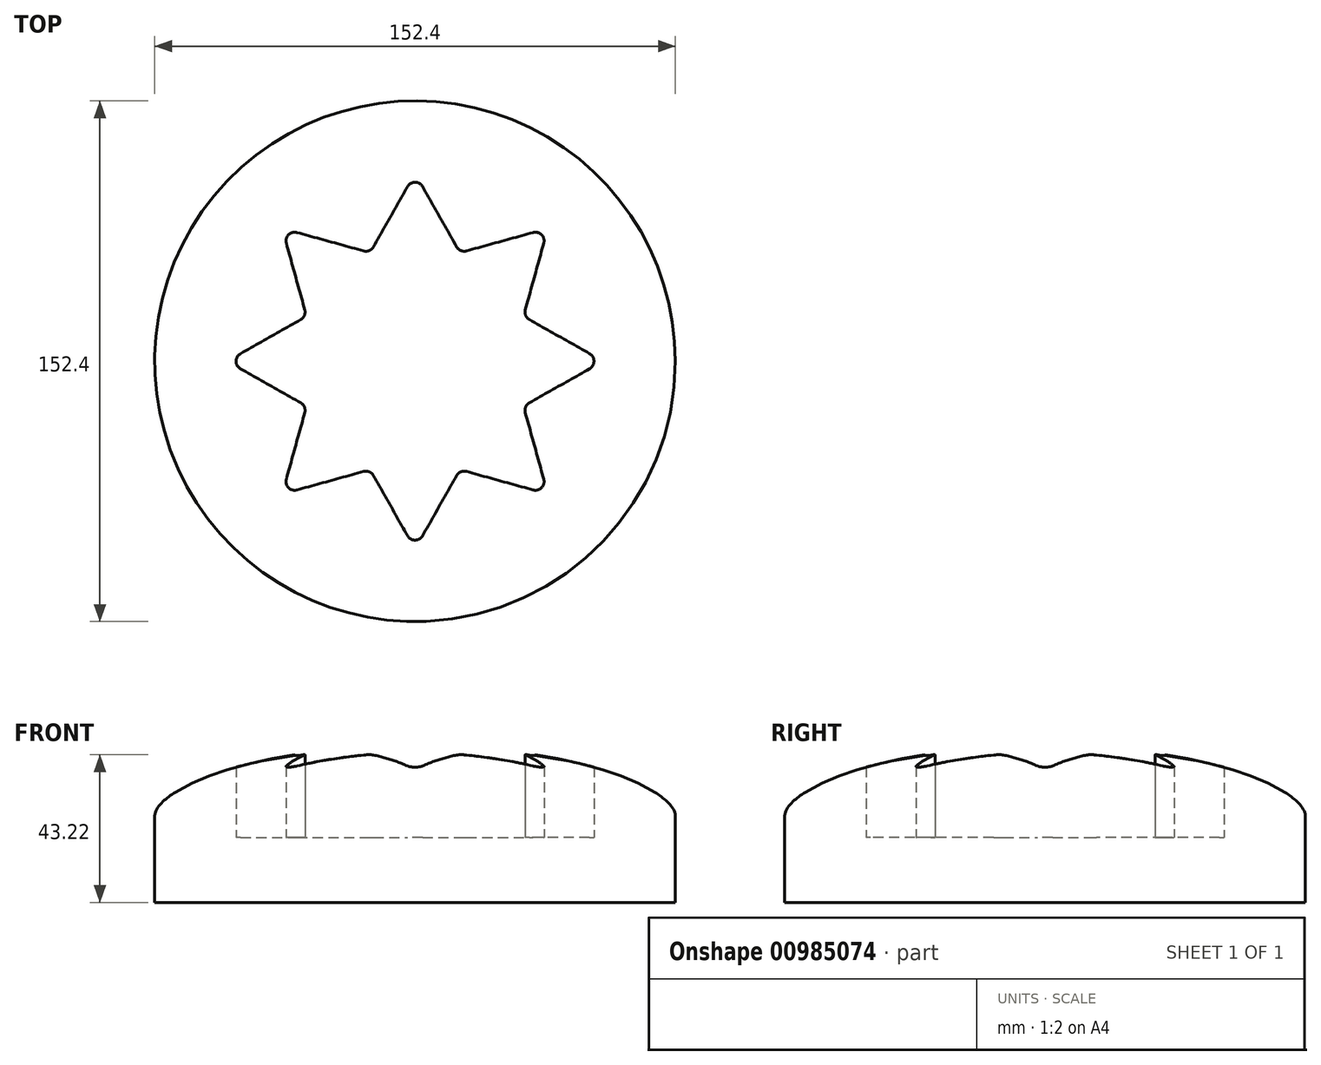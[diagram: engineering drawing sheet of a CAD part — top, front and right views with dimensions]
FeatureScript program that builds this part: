
annotation { "Feature Type Name" : "Feature", "Feature Type Description" : "" }
export const myFeature = defineFeature(function(context is Context, id is Id, definition is map)
    precondition{}
    {
        {
            var Q0;
            Q0=qCreatedBy(makeId("Top.planeOp"),FACE);
            var sketch = newSketch(context, id + "F0", { "sketchPlane" : qUnion([Q0])});
            skCircle(sketch, "E0", {"center": v(0, 0) * mm, "radius": 50.8 * mm, "construction": true});
            skCircle(sketch, "E1", {"center": v(0, 0) * mm, "radius": 31.75 * mm, "construction": true});
            skLineSegment(sketch, "E2.0", {"start": v(-13.15, 31.75) * mm, "end": v(13.15, 31.75) * mm, "construction": true});
            skLineSegment(sketch, "E2.1", {"start": v(13.15, 31.75) * mm, "end": v(31.75, 13.15) * mm, "construction": true});
            skLineSegment(sketch, "E2.2", {"start": v(31.75, 13.15) * mm, "end": v(31.75, -13.15) * mm, "construction": true});
            skLineSegment(sketch, "E2.3", {"start": v(31.75, -13.15) * mm, "end": v(13.15, -31.75) * mm, "construction": true});
            skLineSegment(sketch, "E2.4", {"start": v(13.15, -31.75) * mm, "end": v(-13.15, -31.75) * mm, "construction": true});
            skLineSegment(sketch, "E2.5", {"start": v(-13.15, -31.75) * mm, "end": v(-31.75, -13.15) * mm, "construction": true});
            skLineSegment(sketch, "E2.6", {"start": v(-31.75, -13.15) * mm, "end": v(-31.75, 13.15) * mm, "construction": true});
            skLineSegment(sketch, "E2.7", {"start": v(-31.75, 13.15) * mm, "end": v(-13.15, 31.75) * mm, "construction": true});
            skPoint(sketch, "E2.0.midPoint", {"position": v(0, 31.75) * mm});
            skLineSegment(sketch, "E3.0", {"start": v(0, 54.99) * mm, "end": v(38.88, 38.88) * mm, "construction": true});
            skLineSegment(sketch, "E3.1", {"start": v(38.88, 38.88) * mm, "end": v(54.99, 0) * mm, "construction": true});
            skLineSegment(sketch, "E3.2", {"start": v(54.99, 0) * mm, "end": v(38.88, -38.88) * mm, "construction": true});
            skLineSegment(sketch, "E3.3", {"start": v(38.88, -38.88) * mm, "end": v(0, -54.99) * mm, "construction": true});
            skLineSegment(sketch, "E3.4", {"start": v(0, -54.99) * mm, "end": v(-38.88, -38.88) * mm, "construction": true});
            skLineSegment(sketch, "E3.5", {"start": v(-38.88, -38.88) * mm, "end": v(-54.99, 0) * mm, "construction": true});
            skLineSegment(sketch, "E3.6", {"start": v(-54.99, 0) * mm, "end": v(-38.88, 38.88) * mm, "construction": true});
            skLineSegment(sketch, "E3.7", {"start": v(-38.88, 38.88) * mm, "end": v(0, 54.99) * mm, "construction": true});
            skPoint(sketch, "E3.0.midPoint", {"position": v(19.44, 46.93) * mm});
            skLineSegment(sketch, "E4", {"start": v(-12.17, 33.48) * mm, "end": v(-2.21, 51.08) * mm});
            skLineSegment(sketch, "E5", {"start": v(2.21, 51.08) * mm, "end": v(12.17, 33.48) * mm});
            skLineSegment(sketch, "E6", {"start": v(15.06, 32.28) * mm, "end": v(34.56, 37.68) * mm});
            skLineSegment(sketch, "E7", {"start": v(37.68, 34.56) * mm, "end": v(32.28, 15.06) * mm});
            skLineSegment(sketch, "E8", {"start": v(33.48, 12.17) * mm, "end": v(51.08, 2.21) * mm});
            skLineSegment(sketch, "E9", {"start": v(51.08, -2.21) * mm, "end": v(33.48, -12.17) * mm});
            skLineSegment(sketch, "E10", {"start": v(32.28, -15.06) * mm, "end": v(37.68, -34.56) * mm});
            skLineSegment(sketch, "E11", {"start": v(34.56, -37.68) * mm, "end": v(15.06, -32.28) * mm});
            skLineSegment(sketch, "E12", {"start": v(12.17, -33.48) * mm, "end": v(2.21, -51.08) * mm});
            skLineSegment(sketch, "E13", {"start": v(-12.17, -33.48) * mm, "end": v(-2.21, -51.08) * mm});
            skLineSegment(sketch, "E14", {"start": v(-15.06, -32.28) * mm, "end": v(-34.56, -37.68) * mm});
            skLineSegment(sketch, "E15", {"start": v(-32.28, -15.06) * mm, "end": v(-37.68, -34.56) * mm});
            skLineSegment(sketch, "E16", {"start": v(-33.48, -12.17) * mm, "end": v(-51.08, -2.21) * mm});
            skLineSegment(sketch, "E17", {"start": v(-51.08, 2.21) * mm, "end": v(-33.48, 12.17) * mm});
            skLineSegment(sketch, "E18", {"start": v(-32.28, 15.06) * mm, "end": v(-37.68, 34.56) * mm});
            skLineSegment(sketch, "E19", {"start": v(-34.56, 37.68) * mm, "end": v(-15.06, 32.28) * mm});
            skCircle(sketch, "E20", {"center": v(0, 0) * mm, "radius": 76.2 * mm});
            skPoint(sketch, "E21.visualSharp", {"position": v(-31.75, -13.15) * mm});
            skArc(sketch, "E21.filletArc", {"start": v(-32.28, -15.06) * mm, "mid": v(-32.38, -13.41) * mm, "end": v(-33.48, -12.17) * mm});
            skPoint(sketch, "E22.visualSharp", {"position": v(-31.75, 13.15) * mm});
            skArc(sketch, "E22.filletArc", {"start": v(-33.48, 12.17) * mm, "mid": v(-32.38, 13.41) * mm, "end": v(-32.28, 15.06) * mm});
            skPoint(sketch, "E23.visualSharp", {"position": v(-13.15, 31.75) * mm});
            skArc(sketch, "E23.filletArc", {"start": v(-15.06, 32.28) * mm, "mid": v(-13.41, 32.38) * mm, "end": v(-12.17, 33.48) * mm});
            skPoint(sketch, "E24.visualSharp", {"position": v(13.15, 31.75) * mm});
            skArc(sketch, "E24.filletArc", {"start": v(12.17, 33.48) * mm, "mid": v(13.41, 32.38) * mm, "end": v(15.06, 32.28) * mm});
            skPoint(sketch, "E25.visualSharp", {"position": v(31.75, 13.15) * mm});
            skArc(sketch, "E25.filletArc", {"start": v(32.28, 15.06) * mm, "mid": v(32.38, 13.41) * mm, "end": v(33.48, 12.17) * mm});
            skPoint(sketch, "E26.visualSharp", {"position": v(31.75, -13.15) * mm});
            skArc(sketch, "E26.filletArc", {"start": v(33.48, -12.17) * mm, "mid": v(32.38, -13.41) * mm, "end": v(32.28, -15.06) * mm});
            skPoint(sketch, "E27.visualSharp", {"position": v(13.15, -31.75) * mm});
            skArc(sketch, "E27.filletArc", {"start": v(15.06, -32.28) * mm, "mid": v(13.41, -32.38) * mm, "end": v(12.17, -33.48) * mm});
            skPoint(sketch, "E28.visualSharp", {"position": v(-13.15, -31.75) * mm});
            skArc(sketch, "E28.filletArc", {"start": v(-12.17, -33.48) * mm, "mid": v(-13.41, -32.38) * mm, "end": v(-15.06, -32.28) * mm});
            skPoint(sketch, "E29.visualSharp", {"position": v(-54.99, 0) * mm});
            skArc(sketch, "E29.filletArc", {"start": v(-51.08, 2.21) * mm, "mid": v(-52.37, 0) * mm, "end": v(-51.08, -2.21) * mm});
            skPoint(sketch, "E30.visualSharp", {"position": v(-38.88, 38.88) * mm});
            skArc(sketch, "E30.filletArc", {"start": v(-34.56, 37.68) * mm, "mid": v(-37.03, 37.03) * mm, "end": v(-37.68, 34.56) * mm});
            skPoint(sketch, "E31.visualSharp", {"position": v(0, 54.99) * mm});
            skArc(sketch, "E31.filletArc", {"start": v(2.21, 51.08) * mm, "mid": v(0, 52.37) * mm, "end": v(-2.21, 51.08) * mm});
            skPoint(sketch, "E32.visualSharp", {"position": v(38.88, 38.88) * mm});
            skArc(sketch, "E32.filletArc", {"start": v(37.68, 34.56) * mm, "mid": v(37.03, 37.03) * mm, "end": v(34.56, 37.68) * mm});
            skPoint(sketch, "E33.visualSharp", {"position": v(54.99, 0) * mm});
            skArc(sketch, "E33.filletArc", {"start": v(51.08, -2.21) * mm, "mid": v(52.37, 0) * mm, "end": v(51.08, 2.21) * mm});
            skPoint(sketch, "E34.visualSharp", {"position": v(38.88, -38.88) * mm});
            skArc(sketch, "E34.filletArc", {"start": v(34.56, -37.68) * mm, "mid": v(37.03, -37.03) * mm, "end": v(37.68, -34.56) * mm});
            skPoint(sketch, "E35.visualSharp", {"position": v(0, -54.99) * mm});
            skArc(sketch, "E35.filletArc", {"start": v(-2.21, -51.08) * mm, "mid": v(0, -52.37) * mm, "end": v(2.21, -51.08) * mm});
            skPoint(sketch, "E36.visualSharp", {"position": v(-38.88, -38.88) * mm});
            skArc(sketch, "E36.filletArc", {"start": v(-37.68, -34.56) * mm, "mid": v(-37.03, -37.03) * mm, "end": v(-34.56, -37.68) * mm});
            skSolve(sketch);
        }
        {
            var Q0;
            Q0 = qSketchRegion(id + "F0", true);
            var Q1;
            Q1=makeQuery(id+"F0.imprint","IMPRINT",FACE,{"disambiguationData":[TD([[makeQuery(id+"F0.imprint","IMPRINT",EDGE,{"derivedFrom":sQuery(id+"F0.wireOp",EDGE,"E4")}),-1.0]])]});
            extrude(context, id + "F1", {"entities" : qUnion([Q0, Q1]), "oppositeDirection" : true, "depth" : 25.4 * mm, "offsetDistance" : 25.4 * mm});
        }
        {
            var Q0;
            Q0=qCreatedBy(makeId("Right.planeOp"),FACE);
            var sketch = newSketch(context, id + "F2", { "sketchPlane" : qUnion([Q0])});
            skLineSegment(sketch, "E37.0.0", {"start": v(-76.2, 0) * mm, "end": v(76.2, 0) * mm});
            skFitSpline(sketch, "E38", {"points": [v(0, 20.21) * mm, v(-76.2, 0) * mm], "startDerivative": vector(-160.02, 0) * mm, "endDerivative": vector(0, -18.41) * mm});
            skLineSegment(sketch, "E39", {"start": v(0, 20.21) * mm, "end": v(0, 0) * mm});
            skSolve(sketch);
        }
        {
            var Q0;
            Q0 = qSketchRegion(id + "F2", true);
            var Q1;
            Q1=sQuery(id+"F2.wireOp",EDGE,"E39");
            revolve(context, id + "F3", {"operationType" : NewBodyOperationType.ADD, "surfaceOperationType" : NewSurfaceOperationType.NEW, "entities" : qUnion([Q0]), "axis" : qUnion([Q1]), "revolveType" : RevolveType.FULL});
        }
        {
            var Q0;
            Q0=makeQuery(id+"F0.imprint","IMPRINT",FACE,{"disambiguationData":[TD([[makeQuery(id+"F0.imprint","IMPRINT",EDGE,{"derivedFrom":sQuery(id+"F0.wireOp",EDGE,"E4")}),-1.0]])]});
            extrude(context, id + "F4", {"entities" : qUnion([Q0]), "operationType" : NewBodyOperationType.REMOVE, "endBound" : BoundingType.THROUGH_ALL, "depth" : 25.4 * mm, "offsetDistance" : 25.4 * mm, "hasSecondDirection" : true, "secondDirectionOppositeDirection" : true, "secondDirectionDepth" : 6.35 * mm});
        }
    });
